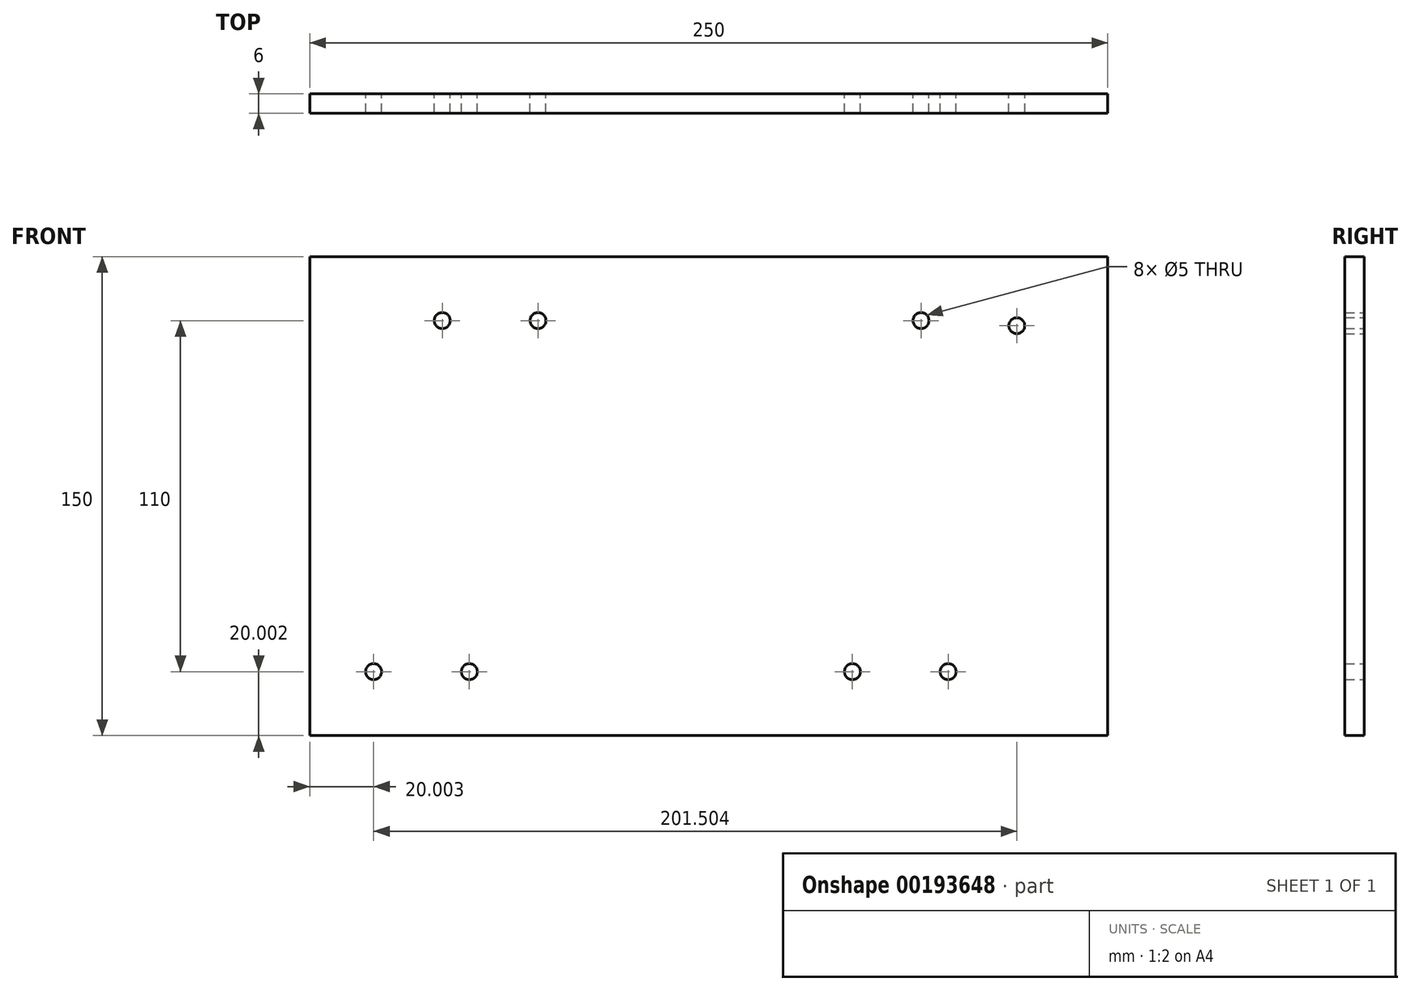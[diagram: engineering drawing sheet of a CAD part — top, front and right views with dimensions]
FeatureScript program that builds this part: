
annotation { "Feature Type Name" : "Feature", "Feature Type Description" : "" }
export const myFeature = defineFeature(function(context is Context, id is Id, definition is map)
    precondition{}
    {
        {
            var Q0;
            Q0=qCreatedBy(makeId("Front.planeOp"),FACE);
            var sketch = newSketch(context, id + "F0", { "sketchPlane" : qUnion([Q0])});
            skLineSegment(sketch, "E0.bottom", {"start": v(-123.9, 35.75) * mm, "end": v(126.1, 35.75) * mm});
            skLineSegment(sketch, "E0.top", {"start": v(-123.9, -114.25) * mm, "end": v(126.1, -114.25) * mm});
            skLineSegment(sketch, "E0.left", {"start": v(-123.9, 35.75) * mm, "end": v(-123.9, -114.25) * mm});
            skLineSegment(sketch, "E0.right", {"start": v(126.1, 35.75) * mm, "end": v(126.1, -114.25) * mm});
            skCircle(sketch, "E1", {"center": v(-82.4, 15.75) * mm, "radius": 2.5 * mm});
            skCircle(sketch, "E2", {"center": v(-52.4, 15.75) * mm, "radius": 2.5 * mm});
            skCircle(sketch, "E3", {"center": v(67.6, 15.75) * mm, "radius": 2.5 * mm});
            skCircle(sketch, "E4", {"center": v(97.6, 14.15) * mm, "radius": 2.5 * mm});
            skCircle(sketch, "E5", {"center": v(76.1, -94.25) * mm, "radius": 2.5 * mm});
            skCircle(sketch, "E6", {"center": v(46.1, -94.25) * mm, "radius": 2.5 * mm});
            skCircle(sketch, "E7", {"center": v(-73.9, -94.25) * mm, "radius": 2.5 * mm});
            skCircle(sketch, "E8", {"center": v(-103.9, -94.25) * mm, "radius": 2.5 * mm});
            skSolve(sketch);
        }
        {
            var Q0;
            Q0 = qSketchRegion(id + "F0", true);
            extrude(context, id + "F1", {"entities" : qUnion([Q0]), "depth" : 6 * mm});
        }
    });
